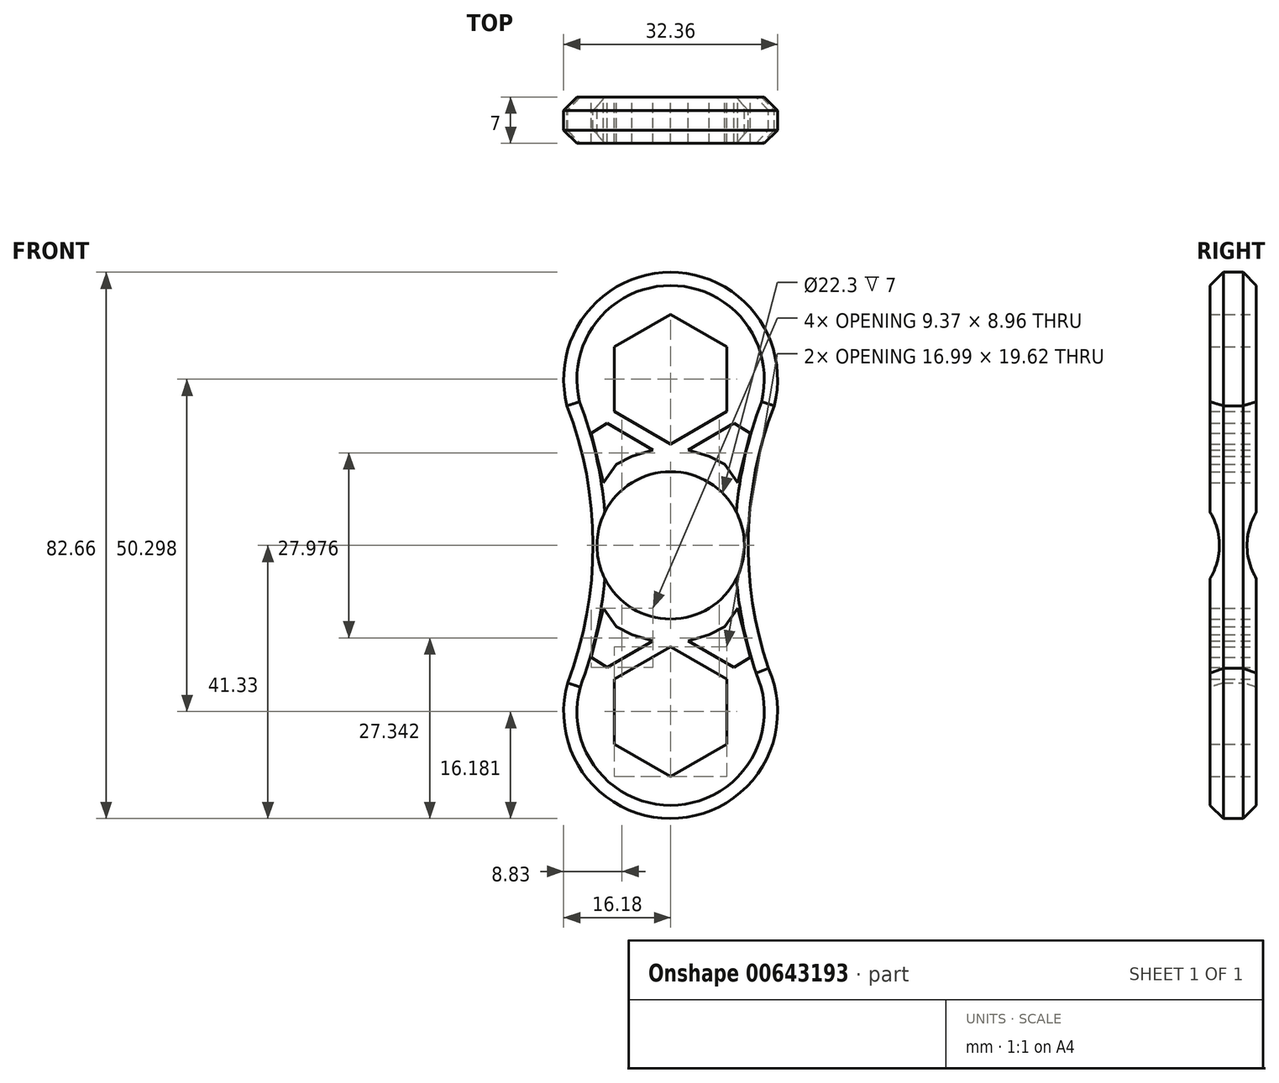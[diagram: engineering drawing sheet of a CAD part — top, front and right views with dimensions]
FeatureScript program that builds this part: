
annotation { "Feature Type Name" : "Feature", "Feature Type Description" : "" }
export const myFeature = defineFeature(function(context is Context, id is Id, definition is map)
    precondition{}
    {
        {
            var Q0;
            Q0=qCreatedBy(makeId("Front.planeOp"),FACE);
            var sketch = newSketch(context, id + "F0", { "sketchPlane" : qUnion([Q0])});
            skPoint(sketch, "E0.center", {"position": v(0, 0) * mm});
            skCircle(sketch, "E1.cCircle", {"center": v(0, 25.15) * mm, "radius": 8.5 * mm, "construction": true});
            skLineSegment(sketch, "E1.0", {"start": v(8.5, 30.05) * mm, "end": v(8.5, 20.24) * mm});
            skLineSegment(sketch, "E1.1", {"start": v(8.5, 20.24) * mm, "end": v(0, 15.34) * mm});
            skLineSegment(sketch, "E1.2", {"start": v(0, 15.34) * mm, "end": v(-8.5, 20.24) * mm});
            skLineSegment(sketch, "E1.3", {"start": v(-8.5, 20.24) * mm, "end": v(-8.5, 30.05) * mm});
            skLineSegment(sketch, "E1.4", {"start": v(-8.5, 30.05) * mm, "end": v(0, 34.96) * mm});
            skLineSegment(sketch, "E1.5", {"start": v(0, 34.96) * mm, "end": v(8.5, 30.05) * mm});
            skPoint(sketch, "E1.0.midPoint", {"position": v(8.5, 25.15) * mm});
            skCircle(sketch, "E2", {"center": v(0, 25.15) * mm, "radius": 16.18 * mm});
            skLineSegment(sketch, "E3.1.0", {"start": v(-8.5, -20.24) * mm, "end": v(0, -15.34) * mm});
            skLineSegment(sketch, "E3.1.1", {"start": v(0, -34.96) * mm, "end": v(-8.5, -30.05) * mm});
            skLineSegment(sketch, "E3.1.2", {"start": v(0, -15.34) * mm, "end": v(8.5, -20.24) * mm});
            skPoint(sketch, "E3.1.3", {"position": v(-8.5, -25.15) * mm});
            skCircle(sketch, "E3.1.4", {"center": v(0, -25.15) * mm, "radius": 8.5 * mm, "construction": true});
            skLineSegment(sketch, "E3.1.5", {"start": v(-8.5, -30.05) * mm, "end": v(-8.5, -20.24) * mm});
            skLineSegment(sketch, "E3.1.6", {"start": v(8.5, -30.05) * mm, "end": v(0, -34.96) * mm});
            skLineSegment(sketch, "E3.1.7", {"start": v(8.5, -20.24) * mm, "end": v(8.5, -30.05) * mm});
            skCircle(sketch, "E3.1.8", {"center": v(0, -25.15) * mm, "radius": 16.18 * mm});
            skCircle(sketch, "E4", {"center": v(0, 0) * mm, "radius": 11.15 * mm});
            skArc(sketch, "E5", {"start": v(-15.58, -20.81) * mm, "mid": v(-11.74, 0.17) * mm, "end": v(-15.67, 21.13) * mm});
            skArc(sketch, "E6.MirrorCS", {"start": v(15.58, -20.81) * mm, "mid": v(11.74, 0.17) * mm, "end": v(15.67, 21.13) * mm});
            skLineSegment(sketch, "E7", {"start": v(2.66, 14.46) * mm, "end": v(9.6, 18.47) * mm});
            skLineSegment(sketch, "E8", {"start": v(9.6, 18.47) * mm, "end": v(12.04, 16.94) * mm});
            skLineSegment(sketch, "E9", {"start": v(12.04, 16.94) * mm, "end": v(10.18, 9.5) * mm});
            skLineSegment(sketch, "E10", {"start": v(10.18, 9.5) * mm, "end": v(8.19, 12.28) * mm});
            skLineSegment(sketch, "E11", {"start": v(8.19, 12.28) * mm, "end": v(5.86, 13.5) * mm});
            skLineSegment(sketch, "E12", {"start": v(5.86, 13.5) * mm, "end": v(2.66, 14.46) * mm});
            skLineSegment(sketch, "E13.MirrorCS", {"start": v(-9.6, 18.47) * mm, "end": v(-12.04, 16.94) * mm});
            skLineSegment(sketch, "E14.MirrorCS", {"start": v(-8.19, 12.28) * mm, "end": v(-5.86, 13.5) * mm});
            skLineSegment(sketch, "E15.MirrorCS", {"start": v(-5.86, 13.5) * mm, "end": v(-2.66, 14.46) * mm});
            skLineSegment(sketch, "E16.MirrorCS", {"start": v(-2.66, 14.46) * mm, "end": v(-9.6, 18.47) * mm});
            skLineSegment(sketch, "E17.MirrorCS", {"start": v(-12.04, 16.94) * mm, "end": v(-10.18, 9.5) * mm});
            skLineSegment(sketch, "E18.MirrorCS", {"start": v(-10.18, 9.5) * mm, "end": v(-8.19, 12.28) * mm});
            skLineSegment(sketch, "E19.MirrorCS", {"start": v(-10.18, -9.5) * mm, "end": v(-8.19, -12.28) * mm});
            skLineSegment(sketch, "E20.MirrorCS", {"start": v(-2.66, -14.46) * mm, "end": v(-9.6, -18.47) * mm});
            skLineSegment(sketch, "E21.MirrorCS", {"start": v(-12.04, -16.94) * mm, "end": v(-10.18, -9.5) * mm});
            skLineSegment(sketch, "E22.MirrorCS", {"start": v(-5.86, -13.5) * mm, "end": v(-2.66, -14.46) * mm});
            skLineSegment(sketch, "E23.MirrorCS", {"start": v(-8.19, -12.28) * mm, "end": v(-5.86, -13.5) * mm});
            skLineSegment(sketch, "E24.MirrorCS", {"start": v(-9.6, -18.47) * mm, "end": v(-12.04, -16.94) * mm});
            skLineSegment(sketch, "E25.MirrorCS", {"start": v(8.19, -12.28) * mm, "end": v(5.86, -13.5) * mm});
            skLineSegment(sketch, "E26.MirrorCS", {"start": v(9.6, -18.47) * mm, "end": v(12.04, -16.94) * mm});
            skLineSegment(sketch, "E27.MirrorCS", {"start": v(5.86, -13.5) * mm, "end": v(2.66, -14.46) * mm});
            skLineSegment(sketch, "E28.MirrorCS", {"start": v(2.66, -14.46) * mm, "end": v(9.6, -18.47) * mm});
            skLineSegment(sketch, "E29.MirrorCS", {"start": v(12.04, -16.94) * mm, "end": v(10.18, -9.5) * mm});
            skLineSegment(sketch, "E30.MirrorCS", {"start": v(10.18, -9.5) * mm, "end": v(8.19, -12.28) * mm});
            skSolve(sketch);
        }
        {
            var Q0;
            Q0=makeQuery(id+"F0.imprint","IMPRINT",FACE,{"disambiguationData":[TD([[makeQuery(id+"F0.imprint","IMPRINT",EDGE,{"derivedFrom":sQuery(id+"F0.wireOp",EDGE,"E1.0")}),1.0]])]});
            var Q1;
            {var subQ0=sQuery(id+"F0.wireOp",EDGE,"E6.MirrorCS");var subQ1=sQuery(id+"F0.wireOp",EDGE,"E2");var subQ2=makeQuery(id+"F0.imprint","INTERSECT",VERTEX,{"disambiguationData":[OD(1.0)],"derivedFrom":[subQ1,subQ0]});Q1=makeQuery(id+"F0.imprint","IMPRINT",FACE,{"disambiguationData":[TD([[makeQuery(id+"F0.imprint","IMPRINT",EDGE,{"disambiguationData":[TD([[subQ2,1.0]])],"derivedFrom":subQ1}),-1.0]])]});}
            var Q2;
            {var subQ0=sQuery(id+"F0.wireOp",EDGE,"E5");var subQ1=sQuery(id+"F0.wireOp",EDGE,"E2");var subQ2=makeQuery(id+"F0.imprint","INTERSECT",VERTEX,{"disambiguationData":[OD(1.0)],"derivedFrom":[subQ1,subQ0]});Q2=makeQuery(id+"F0.imprint","IMPRINT",FACE,{"disambiguationData":[TD([[makeQuery(id+"F0.imprint","IMPRINT",EDGE,{"disambiguationData":[TD([[subQ2,-1.0]])],"derivedFrom":subQ1}),-1.0]])]});}
            var Q3;
            Q3=makeQuery(id+"F0.imprint","IMPRINT",FACE,{"disambiguationData":[TD([[makeQuery(id+"F0.imprint","IMPRINT",EDGE,{"derivedFrom":sQuery(id+"F0.wireOp",EDGE,"E3.1.0")}),1.0]])]});
            extrude(context, id + "F1", {"entities" : qUnion([Q0, Q1, Q2, Q3]), "depth" : 7 * mm, "offsetDistance" : 25 * mm});
        }
        {
            var Q0;
            Q0=makeQuery(id+"F1.opExtrude","CAP_EDGE",EDGE,{"disambiguationData":[OSD([sQuery(id+"F0.wireOp",EDGE,"E6.MirrorCS")])],"isStart":true});
            var Q1;
            Q1=makeQuery(id+"F1.opExtrude","CAP_EDGE",EDGE,{"disambiguationData":[OSD([sQuery(id+"F0.wireOp",EDGE,"E5")])],"isStart":true});
            var Q2;
            Q2=makeQuery(id+"F1.opExtrude","CAP_EDGE",EDGE,{"disambiguationData":[OSD([sQuery(id+"F0.wireOp",EDGE,"E5")])],"isStart":false});
            var Q3;
            Q3=makeQuery(id+"F1.opExtrude","CAP_EDGE",EDGE,{"disambiguationData":[OSD([sQuery(id+"F0.wireOp",EDGE,"E6.MirrorCS")])],"isStart":false});
            var Q4;
            Q4=makeQuery(id+"F1.opExtrude","CAP_EDGE",EDGE,{"disambiguationData":[OSD([sQuery(id+"F0.wireOp",EDGE,"E2")])],"isStart":false});
            var Q5;
            Q5=makeQuery(id+"F1.opExtrude","CAP_EDGE",EDGE,{"disambiguationData":[OSD([sQuery(id+"F0.wireOp",EDGE,"E2")])],"isStart":true});
            var Q6;
            Q6=makeQuery(id+"F1.opExtrude","CAP_EDGE",EDGE,{"disambiguationData":[OSD([sQuery(id+"F0.wireOp",EDGE,"E3.1.8")])],"isStart":false});
            var Q7;
            Q7=makeQuery(id+"F1.opExtrude","CAP_EDGE",EDGE,{"disambiguationData":[OSD([sQuery(id+"F0.wireOp",EDGE,"E3.1.8")])],"isStart":true});
            chamfer(context, id + "F2", {"entities" : qUnion([Q0, Q1, Q2, Q3, Q4, Q5, Q6, Q7]), "width" : 2 * mm, "tangentPropagation" : true});
        }
    });
